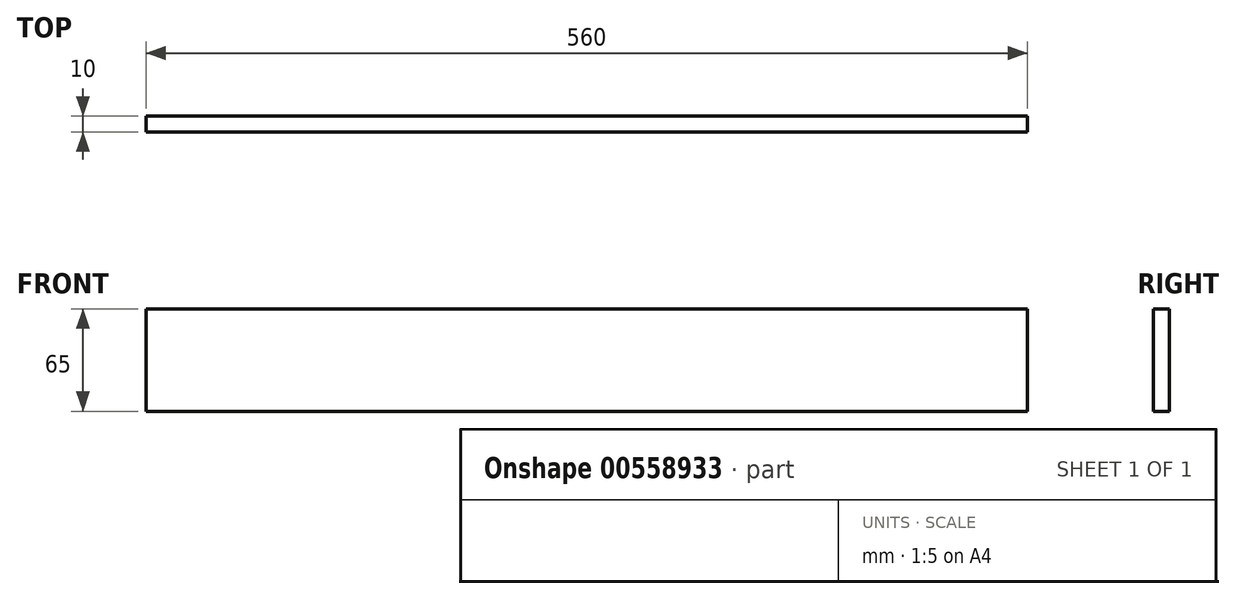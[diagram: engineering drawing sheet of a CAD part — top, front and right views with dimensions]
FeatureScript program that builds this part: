
annotation { "Feature Type Name" : "Feature", "Feature Type Description" : "" }
export const myFeature = defineFeature(function(context is Context, id is Id, definition is map)
    precondition{}
    {
        {
            var Q0;
            Q0=qCreatedBy(makeId("Front.planeOp"),FACE);
            var sketch = newSketch(context, id + "F0", { "sketchPlane" : qUnion([Q0])});
            skLineSegment(sketch, "E0.bottom", {"start": v(280, -32.5) * mm, "end": v(-280, -32.5) * mm});
            skLineSegment(sketch, "E0.top", {"start": v(280, 32.5) * mm, "end": v(-280, 32.5) * mm});
            skLineSegment(sketch, "E0.left", {"start": v(280, -32.5) * mm, "end": v(280, 32.5) * mm});
            skLineSegment(sketch, "E0.right", {"start": v(-280, -32.5) * mm, "end": v(-280, 32.5) * mm});
            skPoint(sketch, "E0.middle", {"position": v(0, 0) * mm});
            skSolve(sketch);
        }
        {
            var Q0;
            Q0 = qSketchRegion(id + "F0", true);
            extrude(context, id + "F1", {"entities" : qUnion([Q0]), "depth" : 10 * mm, "offsetDistance" : 25 * mm});
        }
    });
